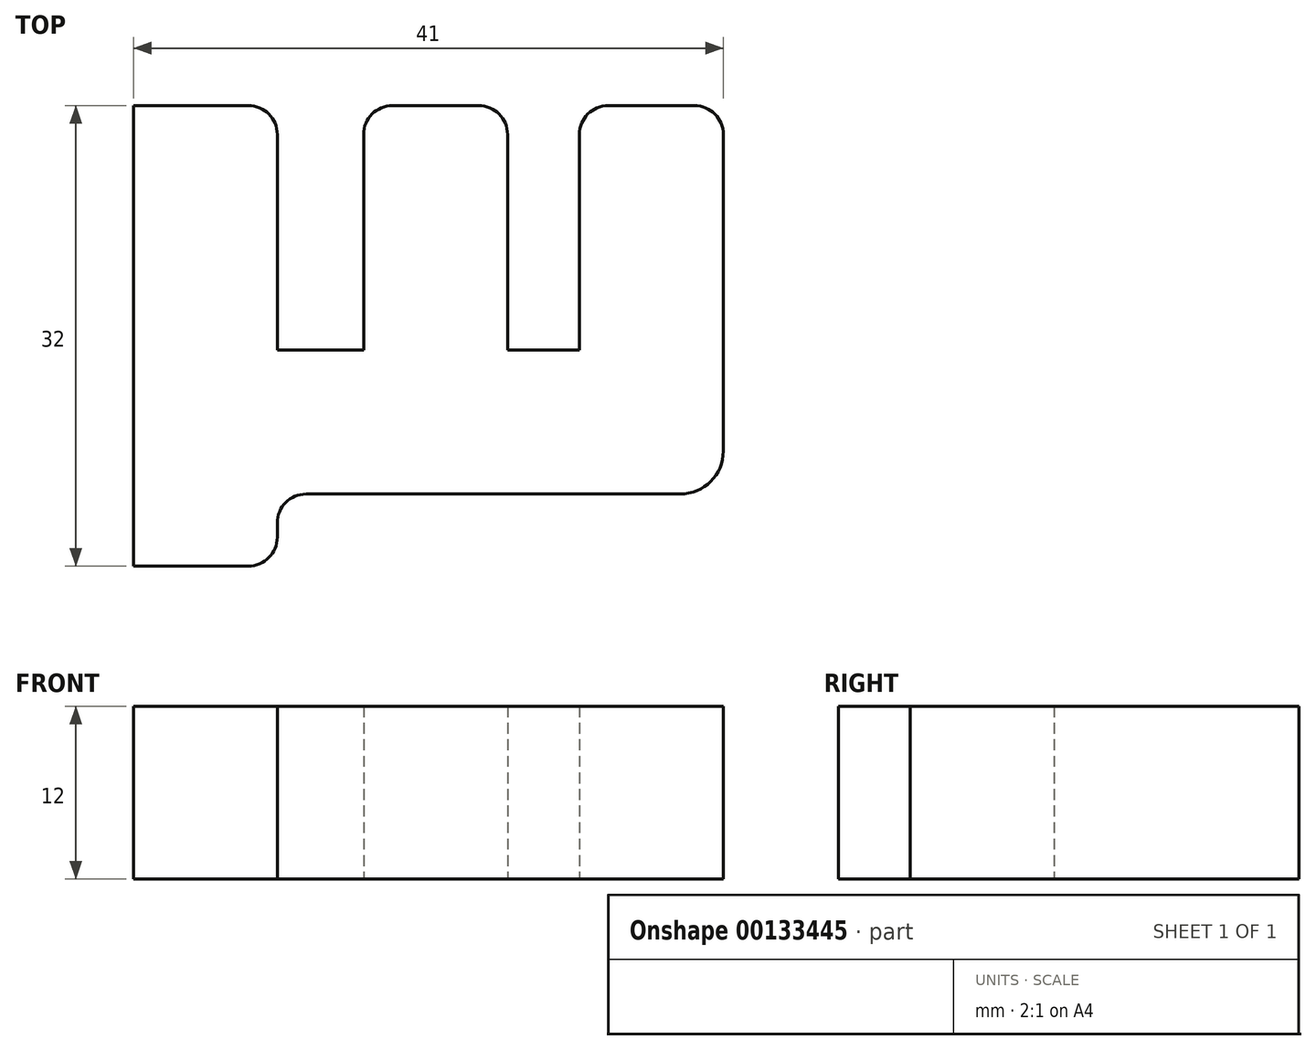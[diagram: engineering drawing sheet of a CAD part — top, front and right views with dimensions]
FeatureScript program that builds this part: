
annotation { "Feature Type Name" : "Feature", "Feature Type Description" : "" }
export const myFeature = defineFeature(function(context is Context, id is Id, definition is map)
    precondition{}
    {
        {
            var Q0;
            Q0=qCreatedBy(makeId("Top.planeOp"),FACE);
            var sketch = newSketch(context, id + "F0", { "sketchPlane" : qUnion([Q0])});
            skLineSegment(sketch, "E0.bottom", {"start": v(-29.8, -15.72) * mm, "end": v(-21.8, -15.72) * mm});
            skLineSegment(sketch, "E0.top", {"start": v(-17.8, -42.72) * mm, "end": v(8.2, -42.72) * mm});
            skLineSegment(sketch, "E0.left", {"start": v(-29.8, -15.72) * mm, "end": v(-29.8, -42.72) * mm});
            skLineSegment(sketch, "E0.right", {"start": v(11.2, -17.72) * mm, "end": v(11.2, -39.72) * mm});
            skLineSegment(sketch, "E1", {"start": v(-19.8, -17.72) * mm, "end": v(-19.8, -32.72) * mm});
            skLineSegment(sketch, "E2", {"start": v(-19.8, -32.72) * mm, "end": v(-13.8, -32.72) * mm});
            skLineSegment(sketch, "E3", {"start": v(-13.8, -32.72) * mm, "end": v(-13.8, -17.72) * mm});
            skLineSegment(sketch, "E4", {"start": v(-3.8, -17.72) * mm, "end": v(-3.8, -32.72) * mm});
            skLineSegment(sketch, "E5", {"start": v(-3.8, -32.72) * mm, "end": v(1.2, -32.72) * mm});
            skLineSegment(sketch, "E6", {"start": v(1.2, -32.72) * mm, "end": v(1.2, -17.72) * mm});
            skLineSegment(sketch, "E7.trimOffspring", {"start": v(-11.8, -15.72) * mm, "end": v(-5.8, -15.72) * mm});
            skLineSegment(sketch, "E8.trimOffspring", {"start": v(3.2, -15.72) * mm, "end": v(9.2, -15.72) * mm});
            skPoint(sketch, "E9.visualSharp", {"position": v(-19.8, -15.72) * mm});
            skArc(sketch, "E9.filletArc", {"start": v(-19.8, -17.72) * mm, "mid": v(-20.38, -16.3) * mm, "end": v(-21.8, -15.72) * mm});
            skPoint(sketch, "E10.visualSharp", {"position": v(-13.8, -15.72) * mm});
            skArc(sketch, "E10.filletArc", {"start": v(-11.8, -15.72) * mm, "mid": v(-13.21, -16.3) * mm, "end": v(-13.8, -17.72) * mm});
            skPoint(sketch, "E11.visualSharp", {"position": v(-3.8, -15.72) * mm});
            skArc(sketch, "E11.filletArc", {"start": v(-3.8, -17.72) * mm, "mid": v(-4.38, -16.3) * mm, "end": v(-5.8, -15.72) * mm});
            skPoint(sketch, "E12.visualSharp", {"position": v(1.2, -15.72) * mm});
            skArc(sketch, "E12.filletArc", {"start": v(3.2, -15.72) * mm, "mid": v(1.79, -16.3) * mm, "end": v(1.2, -17.72) * mm});
            skPoint(sketch, "E13.visualSharp", {"position": v(11.2, -15.72) * mm});
            skArc(sketch, "E13.filletArc", {"start": v(11.2, -17.72) * mm, "mid": v(10.62, -16.3) * mm, "end": v(9.2, -15.72) * mm});
            skPoint(sketch, "E14.visualSharp", {"position": v(11.2, -42.72) * mm});
            skArc(sketch, "E14.filletArc", {"start": v(8.2, -42.72) * mm, "mid": v(10.32, -41.84) * mm, "end": v(11.2, -39.72) * mm});
            skLineSegment(sketch, "E15", {"start": v(-29.8, -42.72) * mm, "end": v(-29.8, -47.72) * mm});
            skLineSegment(sketch, "E16", {"start": v(-29.8, -47.72) * mm, "end": v(-21.8, -47.72) * mm});
            skLineSegment(sketch, "E17", {"start": v(-19.8, -45.72) * mm, "end": v(-19.8, -44.72) * mm});
            skPoint(sketch, "E18.visualSharp", {"position": v(-19.8, -42.72) * mm});
            skArc(sketch, "E18.filletArc", {"start": v(-17.8, -42.72) * mm, "mid": v(-19.21, -43.3) * mm, "end": v(-19.8, -44.72) * mm});
            skPoint(sketch, "E19.visualSharp", {"position": v(-19.8, -47.72) * mm});
            skArc(sketch, "E19.filletArc", {"start": v(-21.8, -47.72) * mm, "mid": v(-20.38, -47.13) * mm, "end": v(-19.8, -45.72) * mm});
            skSolve(sketch);
        }
        {
            var Q0;
            Q0=makeQuery(id+"F0.imprint","IMPRINT",FACE,{"disambiguationData":[TD([[makeQuery(id+"F0.imprint","IMPRINT",EDGE,{"derivedFrom":sQuery(id+"F0.wireOp",EDGE,"E0.bottom")}),-1.0]])]});
            extrude(context, id + "F1", {"entities" : qUnion([Q0]), "depth" : 12 * mm});
        }
    });
